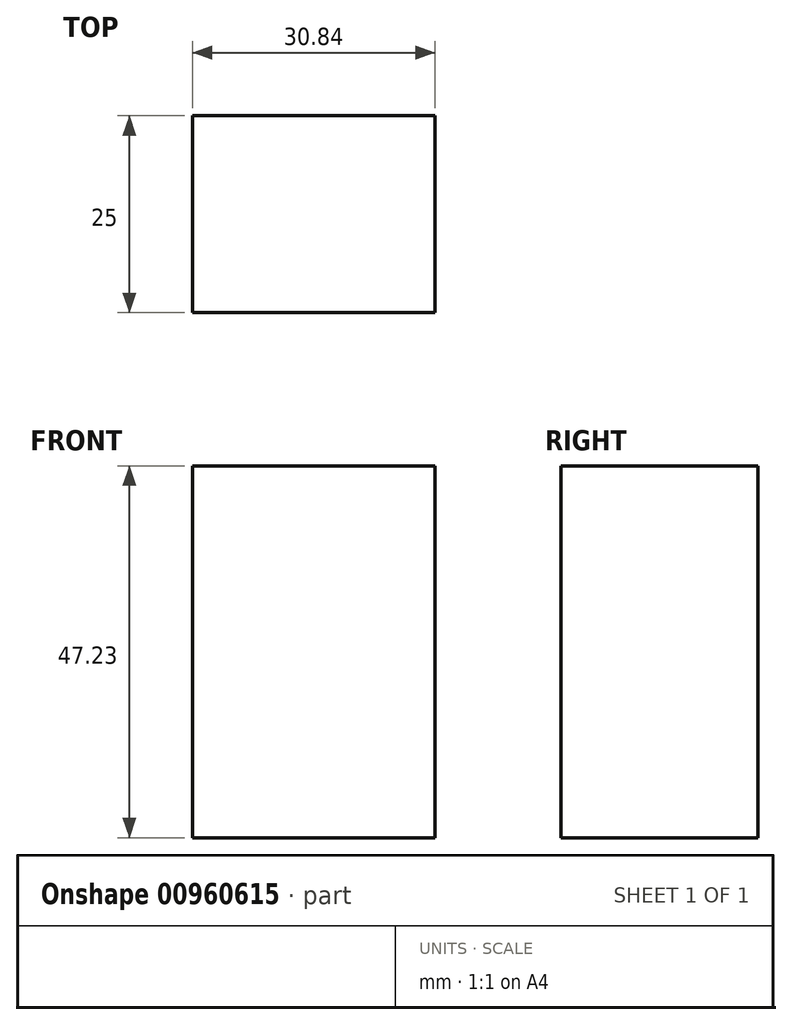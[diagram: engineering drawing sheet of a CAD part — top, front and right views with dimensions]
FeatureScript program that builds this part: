
annotation { "Feature Type Name" : "Feature", "Feature Type Description" : "" }
export const myFeature = defineFeature(function(context is Context, id is Id, definition is map)
    precondition{}
    {
        {
            var Q0;
            Q0=qCreatedBy(makeId("Front.planeOp"),FACE);
            var sketch = newSketch(context, id + "F0", { "sketchPlane" : qUnion([Q0])});
            skLineSegment(sketch, "E0.bottom", {"start": v(-10.96, 0) * mm, "end": v(19.88, 0) * mm});
            skLineSegment(sketch, "E0.top", {"start": v(-10.96, 47.23) * mm, "end": v(19.88, 47.23) * mm});
            skLineSegment(sketch, "E0.left", {"start": v(-10.96, 0) * mm, "end": v(-10.96, 47.23) * mm});
            skLineSegment(sketch, "E0.right", {"start": v(19.88, 0) * mm, "end": v(19.88, 47.23) * mm});
            skSolve(sketch);
        }
        {
            var Q0;
            Q0 = qSketchRegion(id + "F0", true);
            extrude(context, id + "F1", {"entities" : qUnion([Q0]), "depth" : 25 * mm, "offsetDistance" : 25 * mm});
        }
    });
